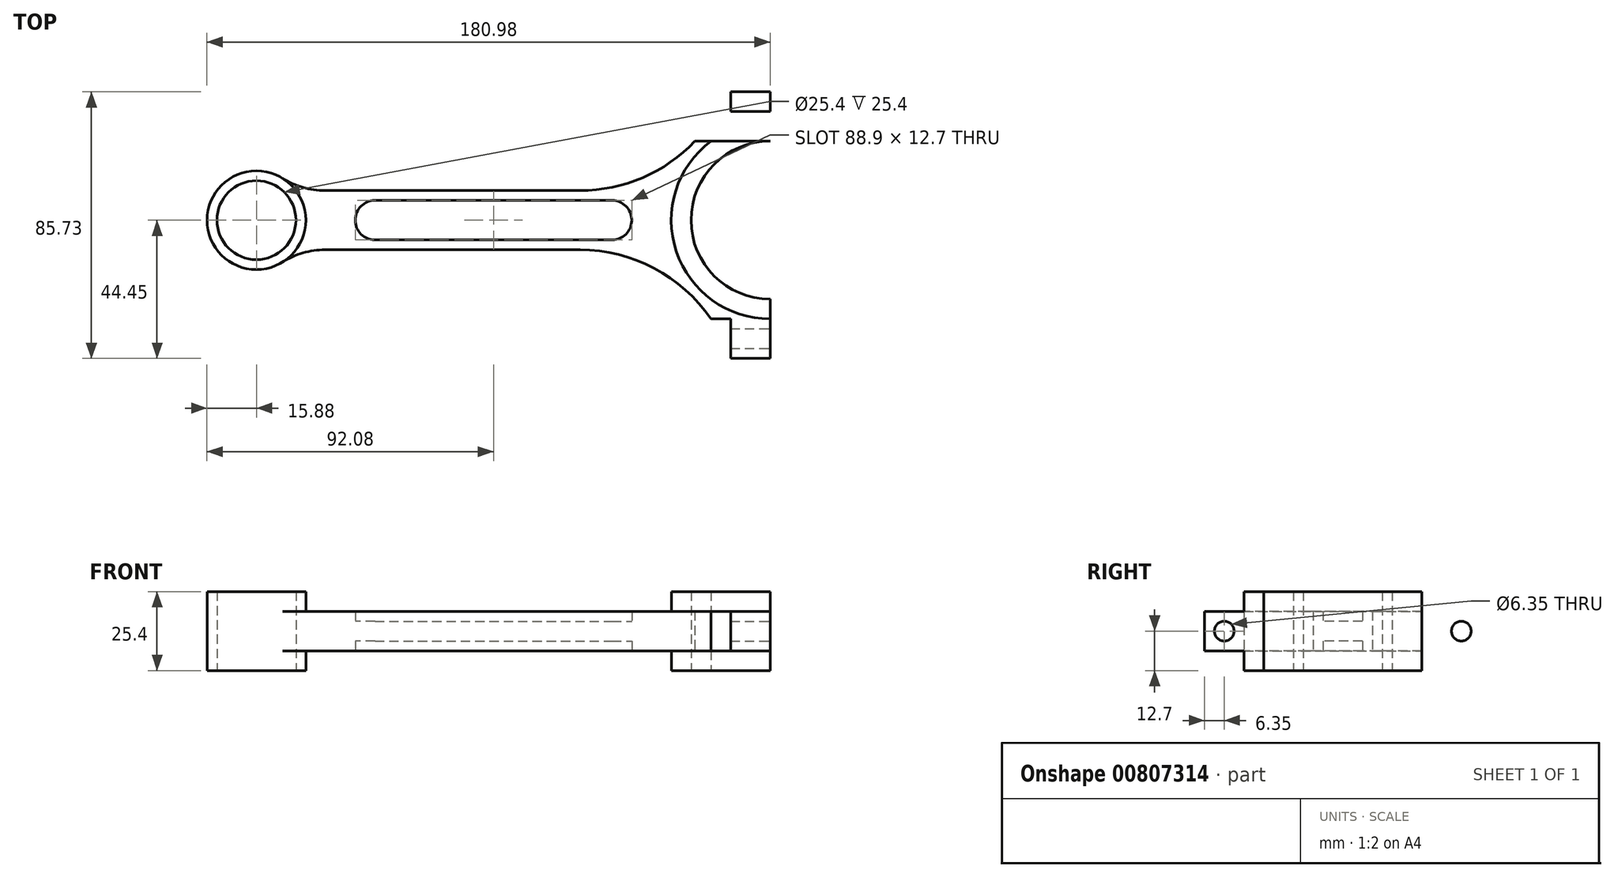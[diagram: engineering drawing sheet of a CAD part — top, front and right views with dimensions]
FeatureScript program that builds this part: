
annotation { "Feature Type Name" : "Feature", "Feature Type Description" : "" }
export const myFeature = defineFeature(function(context is Context, id is Id, definition is map)
    precondition{}
    {
        {
            var Q0;
            Q0=qCreatedBy(makeId("Top.planeOp"),FACE);
            var sketch = newSketch(context, id + "F0", { "sketchPlane" : qUnion([Q0])});
            skLineSegment(sketch, "E0", {"start": v(0, 31.75) * mm, "end": v(0, 25.4) * mm});
            skArc(sketch, "E1", {"start": v(0, 31.75) * mm, "mid": v(-31.75, 0) * mm, "end": v(0, -31.75) * mm});
            skLineSegment(sketch, "E2", {"start": v(0, -25.4) * mm, "end": v(0, -31.75) * mm});
            skLineSegment(sketch, "E3", {"start": v(0, 25.4) * mm, "end": v(0, 25.4) * mm});
            skArc(sketch, "E4", {"start": v(0, 25.4) * mm, "mid": v(-25.4, 0) * mm, "end": v(0, -25.4) * mm});
            skLineSegment(sketch, "E5", {"start": v(0, 25.4) * mm, "end": v(0, 44.45) * mm});
            skPoint(sketch, "E5.endSnap0", {"position": v(0, 28.58) * mm});
            skLineSegment(sketch, "E6", {"start": v(0, -25.4) * mm, "end": v(0, -44.45) * mm});
            skLineSegment(sketch, "E7", {"start": v(-171.56, 0) * mm, "end": v(9.28, 0) * mm, "construction": true});
            skLineSegment(sketch, "E8", {"start": v(0, 44.45) * mm, "end": v(-12.7, 44.45) * mm});
            skLineSegment(sketch, "E9", {"start": v(-12.7, 44.45) * mm, "end": v(-12.7, 31.75) * mm});
            skLineSegment(sketch, "E10", {"start": v(-12.7, 31.75) * mm, "end": v(-19.05, 31.75) * mm});
            skLineSegment(sketch, "E11.MirrorCS", {"start": v(-12.7, -31.75) * mm, "end": v(-19.05, -31.75) * mm});
            skLineSegment(sketch, "E12.MirrorCS", {"start": v(0, -44.45) * mm, "end": v(-12.7, -44.45) * mm});
            skLineSegment(sketch, "E13.MirrorCS", {"start": v(-12.7, -44.45) * mm, "end": v(-12.7, -31.75) * mm});
            skCircle(sketch, "E14", {"center": v(-165.1, 0) * mm, "radius": 12.7 * mm});
            skCircle(sketch, "E15", {"center": v(-165.1, 0) * mm, "radius": 15.88 * mm});
            skLineSegment(sketch, "E16", {"start": v(-143.1, 9.52) * mm, "end": v(-61.05, 9.52) * mm});
            skArc(sketch, "E17", {"start": v(-61.05, 9.52) * mm, "mid": v(-37.3, 15.42) * mm, "end": v(-19.05, 31.75) * mm});
            skArc(sketch, "E18", {"start": v(-156.64, 13.43) * mm, "mid": v(-150.15, 10.52) * mm, "end": v(-143.1, 9.53) * mm});
            skArc(sketch, "E19.MirrorCS", {"start": v(-156.64, -13.43) * mm, "mid": v(-150.15, -10.52) * mm, "end": v(-143.1, -9.53) * mm});
            skLineSegment(sketch, "E20.MirrorCS", {"start": v(-143.1, -9.52) * mm, "end": v(-61.05, -9.52) * mm});
            skArc(sketch, "E21.MirrorCS", {"start": v(-61.05, -9.52) * mm, "mid": v(-37.3, -15.42) * mm, "end": v(-19.05, -31.75) * mm});
            skPoint(sketch, "E22", {"position": v(-127, 0) * mm});
            skPoint(sketch, "E23", {"position": v(-50.8, 0) * mm});
            skLineSegment(sketch, "E24", {"start": v(-127, 6.35) * mm, "end": v(-50.8, 6.35) * mm});
            skLineSegment(sketch, "E25.MirrorCS", {"start": v(-127, -6.35) * mm, "end": v(-50.8, -6.35) * mm});
            skArc(sketch, "E26", {"start": v(-127, 6.35) * mm, "mid": v(-133.35, 0) * mm, "end": v(-127, -6.35) * mm});
            skArc(sketch, "E27", {"start": v(-50.8, -6.35) * mm, "mid": v(-44.45, 0) * mm, "end": v(-50.8, 6.35) * mm});
            skSolve(sketch);
        }
        {
            var Q0;
            {var subQ1=sQuery(id+"F0.wireOp",EDGE,"E1");Q0=makeQuery(id+"F0.imprint","IMPRINT",FACE,{"disambiguationData":[TD([[makeQuery(id+"F0.imprint","IMPRINT",EDGE,{"derivedFrom":subQ1}),-1.0]])]});}
            extrude(context, id + "F1", {"entities" : qUnion([Q0]), "endBound" : BoundingType.SYMMETRIC, "depth" : 12.7 * mm, "offsetDistance" : 25.4 * mm});
        }
        {
            var Q0;
            Q0=makeQuery(id+"F0.imprint","IMPRINT",FACE,{"disambiguationData":[TD([[makeQuery(id+"F0.imprint","IMPRINT",EDGE,{"derivedFrom":sQuery(id+"F0.wireOp",EDGE,"E14")}),-1.0]])]});
            var Q1;
            {var subQ0=sQuery(id+"F0.wireOp",EDGE,"E1");Q1=makeQuery(id+"F0.imprint","IMPRINT",FACE,{"disambiguationData":[TD([[makeQuery(id+"F0.imprint","IMPRINT",EDGE,{"derivedFrom":subQ0}),1.0]])]});}
            extrude(context, id + "F2", {"entities" : qUnion([Q0, Q1]), "operationType" : NewBodyOperationType.ADD, "endBound" : BoundingType.SYMMETRIC, "depth" : 25.4 * mm, "offsetDistance" : 25.4 * mm});
        }
        {
            var Q0;
            Q0=makeQuery(id+"F0.imprint","IMPRINT",FACE,{"disambiguationData":[TD([[makeQuery(id+"F0.imprint","IMPRINT",EDGE,{"derivedFrom":sQuery(id+"F0.wireOp",EDGE,"E24")}),-1.0]])]});
            extrude(context, id + "F3", {"entities" : qUnion([Q0]), "operationType" : NewBodyOperationType.ADD, "endBound" : BoundingType.SYMMETRIC, "depth" : 6.35 * mm, "offsetDistance" : 25.4 * mm});
        }
        {
            var Q0;
            {var subQ0=sQuery(id+"F0.wireOp",EDGE,"E6");Q0=makeQuery(id+"F2.boolean.opBoolean","MERGE",FACE,{"derivedFrom":[makeQuery(id+"F1.opExtrude","SWEPT_FACE",FACE,{"disambiguationData":[OSD([subQ0])]}),makeQuery(id+"F2.opExtrude","SWEPT_FACE",FACE,{"disambiguationData":[OSD([subQ0])]})]});}
            var sketch = newSketch(context, id + "F4", { "sketchPlane" : qUnion([Q0])});
            skLineSegment(sketch, "E28.0", {"start": v(-44.45, 6.35) * mm, "end": v(-44.45, -6.35) * mm});
            skLineSegment(sketch, "E29.0", {"start": v(-31.75, 6.35) * mm, "end": v(-44.45, 6.35) * mm});
            skLineSegment(sketch, "E30.0", {"start": v(-31.75, -6.35) * mm, "end": v(-44.45, -6.35) * mm});
            skLineSegment(sketch, "E31.0", {"start": v(-31.75, -6.35) * mm, "end": v(-31.75, -12.7) * mm});
            skLineSegment(sketch, "E32.0", {"start": v(-31.75, 12.7) * mm, "end": v(-31.75, 6.35) * mm});
            skLineSegment(sketch, "E33.0", {"start": v(-25.4, 12.7) * mm, "end": v(-31.75, 12.7) * mm});
            skLineSegment(sketch, "E34.0", {"start": v(-25.4, -12.7) * mm, "end": v(-31.75, -12.7) * mm});
            skLineSegment(sketch, "E35.0", {"start": v(-25.4, 12.7) * mm, "end": v(-25.4, -12.7) * mm});
            skLineSegment(sketch, "E36.0", {"start": v(25.4, 12.7) * mm, "end": v(25.4, -12.7) * mm});
            skLineSegment(sketch, "E37.0", {"start": v(25.4, 12.7) * mm, "end": v(31.75, 12.7) * mm});
            skLineSegment(sketch, "E38.0", {"start": v(25.4, -12.7) * mm, "end": v(31.75, -12.7) * mm});
            skLineSegment(sketch, "E39.0", {"start": v(31.75, -6.35) * mm, "end": v(31.75, -12.7) * mm});
            skLineSegment(sketch, "E40.0", {"start": v(31.75, -6.35) * mm, "end": v(44.45, -6.35) * mm});
            skLineSegment(sketch, "E41.0", {"start": v(44.45, 6.35) * mm, "end": v(44.45, -6.35) * mm});
            skLineSegment(sketch, "E42.0", {"start": v(31.75, 6.35) * mm, "end": v(44.45, 6.35) * mm});
            skLineSegment(sketch, "E43.0", {"start": v(31.75, 12.7) * mm, "end": v(31.75, 6.35) * mm});
            skCircle(sketch, "E44", {"center": v(-38.1, 0) * mm, "radius": 3.18 * mm});
            skLineSegment(sketch, "E45", {"start": v(0, 4.9) * mm, "end": v(0, -4.88) * mm, "construction": true});
            skCircle(sketch, "E46.MirrorC", {"center": v(38.1, 0) * mm, "radius": 3.18 * mm});
            skSolve(sketch);
        }
        {
            var Q0;
            Q0=makeQuery(id+"F4.imprint","IMPRINT",FACE,{"disambiguationData":[TD([[makeQuery(id+"F4.imprint","IMPRINT",EDGE,{"derivedFrom":sQuery(id+"F4.wireOp",EDGE,"E44")}),1.0]])]});
            var Q1;
            Q1=makeQuery(id+"F4.imprint","IMPRINT",FACE,{"disambiguationData":[TD([[makeQuery(id+"F4.imprint","IMPRINT",EDGE,{"derivedFrom":sQuery(id+"F4.wireOp",EDGE,"E46.MirrorC")}),-1.0]])]});
            extrude(context, id + "F5", {"entities" : qUnion([Q0, Q1]), "operationType" : NewBodyOperationType.REMOVE, "endBound" : BoundingType.THROUGH_ALL, "oppositeDirection" : true, "depth" : 25.4 * mm, "offsetDistance" : 25.4 * mm});
        }
    });
